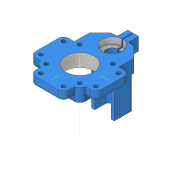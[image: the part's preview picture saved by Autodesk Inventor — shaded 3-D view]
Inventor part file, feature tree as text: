
AUTODESK INVENTOR PART (.ipt)
format: ipt  version: 2020 (Build 240168000, 168)  size: 440,832 bytes
history: native  units: in
note: dims shown in document units (in); Inventor stores cm internally (conversion verified against a paired STEP export)
features: extrude x19, sketch x19, fillet x6, mirror x4, plane x3, pattern_linear x2, other x2, pattern_circular x2, chamfer x1, thicken_offset x1
ambient origin geometry x8: Origin, YZ Plane, XZ Plane, XY Plane, X Axis, Y Axis, Z Axis, Center Point
bodies: Solid1 (feature_tree)
feature tree (59):
  extrude  "Extrusion1"  Depth=2.3622in
  extrude  "Extrusion2"  Depth=0.4724in
  pattern_linear  "Rectangular Pattern1"  Count1=2 Spacing1=1.2205in
  extrude  "Extrusion3"  Depth=1.2205in
  extrude  "Extrusion5"  Depth=1.5453in TaperAngle=0.0deg
  extrude  "Extrusion6"  Depth=0.3937in
  extrude  "Extrusion7"  Depth=0.0394in
  extrude  "Extrusion10"  Depth=0.4724in
  other  "Work Axis1"
  extrude  "Extrusion12"  Depth=0.0394in
  fillet  "Fillet1"  Radius=2.7559in
  fillet  "Fillet3"  Radius=0.0787in
  chamfer  "Chamfer1"  Distance=0.3937in Angle=45.0deg
  extrude  "Extrusion14"  Depth=0.3937in TaperAngle=0.0deg
  plane  "Work Plane1"
  mirror  "Mirror1"
  extrude  "Extrusion15"  Depth=0.5906in
  fillet  "Fillet5"  Radius=0.9055in
  extrude  "Extrusion16"  Depth=0.1181in
  extrude  "Extrusion17"  Depth=1.9685in TaperAngle=0.0deg
  extrude  "Extrusion18"  Depth=0.4921in TaperAngle=0.0deg
  extrude  "Extrusion19"  Depth=0.3937in
  other  "Work Axis2"
  pattern_circular  "Circular Pattern2"  Count=3 Angle=180.0deg
  extrude  "Extrusion20"  Depth=0.315in TaperAngle=0.0deg
  pattern_linear  "Rectangular Pattern2"  Count1=2 Spacing1=0.8268in
  pattern_circular  "Circular Pattern3"  Count=3 Angle=180.0deg
  fillet  "Fillet6"  Radius=0.1969in
  fillet  "Fillet7"  Radius=0.0787in
  fillet  "Fillet8"  Radius=0.0787in
  extrude  "Extrusion21"  Depth=0.7874in TaperAngle=0.0deg
  extrude  "Extrusion22"  Depth=0.1181in TaperAngle=0.0deg
  mirror  "Mirror2"
  plane  "Work Plane2"
  mirror  "Mirror3"
  extrude  "Extrusion23"  [1 undecoded]
  plane  "Work Plane3"
  mirror  "Mirror4"
  extrude  "Extrusion24"  Depth=0.1181in TaperAngle=0.0deg
  thicken_offset  "Thicken1"
  sketch  "Sketch1"  dims[d0=1.6535in d1=2.3622in]
  sketch  "Sketch2"  dims[d2=0.4724in d3=0.0in d4=0.1417in]
  sketch  "Sketch3"  dims[d5=0.4724in d6=0.0in d7=0.7874in d9=1.2205in]
  sketch  "Sketch5"  dims[d10=0.7874in d12=1.2205in d13=0.9055in]
  sketch  "Sketch6"  dims[d14=0.4724in d15=0.0in d19=1.5453in d20=0.0in]
  sketch  "Sketch7"  dims[d21=0.3937in d23=0.3937in]
  sketch  "Sketch10"  dims[d24=0.4724in d25=0.0in d26=0.0394in]
  sketch  "Sketch12"  dims[d27=0.4724in d28=0.0in d35=0.1417in]
  sketch  "Sketch14"  dims[d36=0.3937in d37=0.0in d44=0.0394in d45=2.7559in d46=0.0in d47=0.0787in]
  sketch  "Sketch15"  dims[d49=0.1969in d51=0.3937in d52=0.0787in d53=45.0deg]
  sketch  "Sketch16"  dims[d57=0.3937in d58=1.1811in d59=0.0in]
  sketch  "Sketch17"  dims[d60=-0.8071in d61=0.5906in d62=0.9055in]
  sketch  "Sketch18"  dims[d63=1.4173in d64=0.0in d65=0.1181in]
  sketch  "Sketch20"  dims[d66=1.6535in d67=1.9685in d68=0.0in]
  sketch  "Sketch21"  dims[d69=0.6732in d70=0.4921in d71=0.0in]
  sketch  "Sketch22"  dims[d72=0.4921in d73=0.0in d76=0.3937in]
  sketch  "Sketch23"  dims[d77=0.315in d78=0.0in d79=1.1811in d80=180.0deg]
  sketch  "Sketch24"  dims[d82=0.1417in d83=0.315in d84=0.0in d85=0.7874in d87=0.8268in d88=1.1811in d89=180.0deg d91=0.1969in d92=0.0787in d93=0.0787in]
  sketch  "Sketch25"  dims[d94=1.0236in d95=0.7874in d96=0.0in d98=0.0984in d99=0.0in d100=-0.6102in d102=0.0984in d103=0.0in d104=-0.6102in d105=0.752in d106=0.2362in d107=0.0in d108=0.1181in d109=0.1181in]
note: 1 required parameter value undecoded (feature->parameter linkage not recoverable at this tier; creation-order binding heuristic only, values carry confidence <= 0.55)
